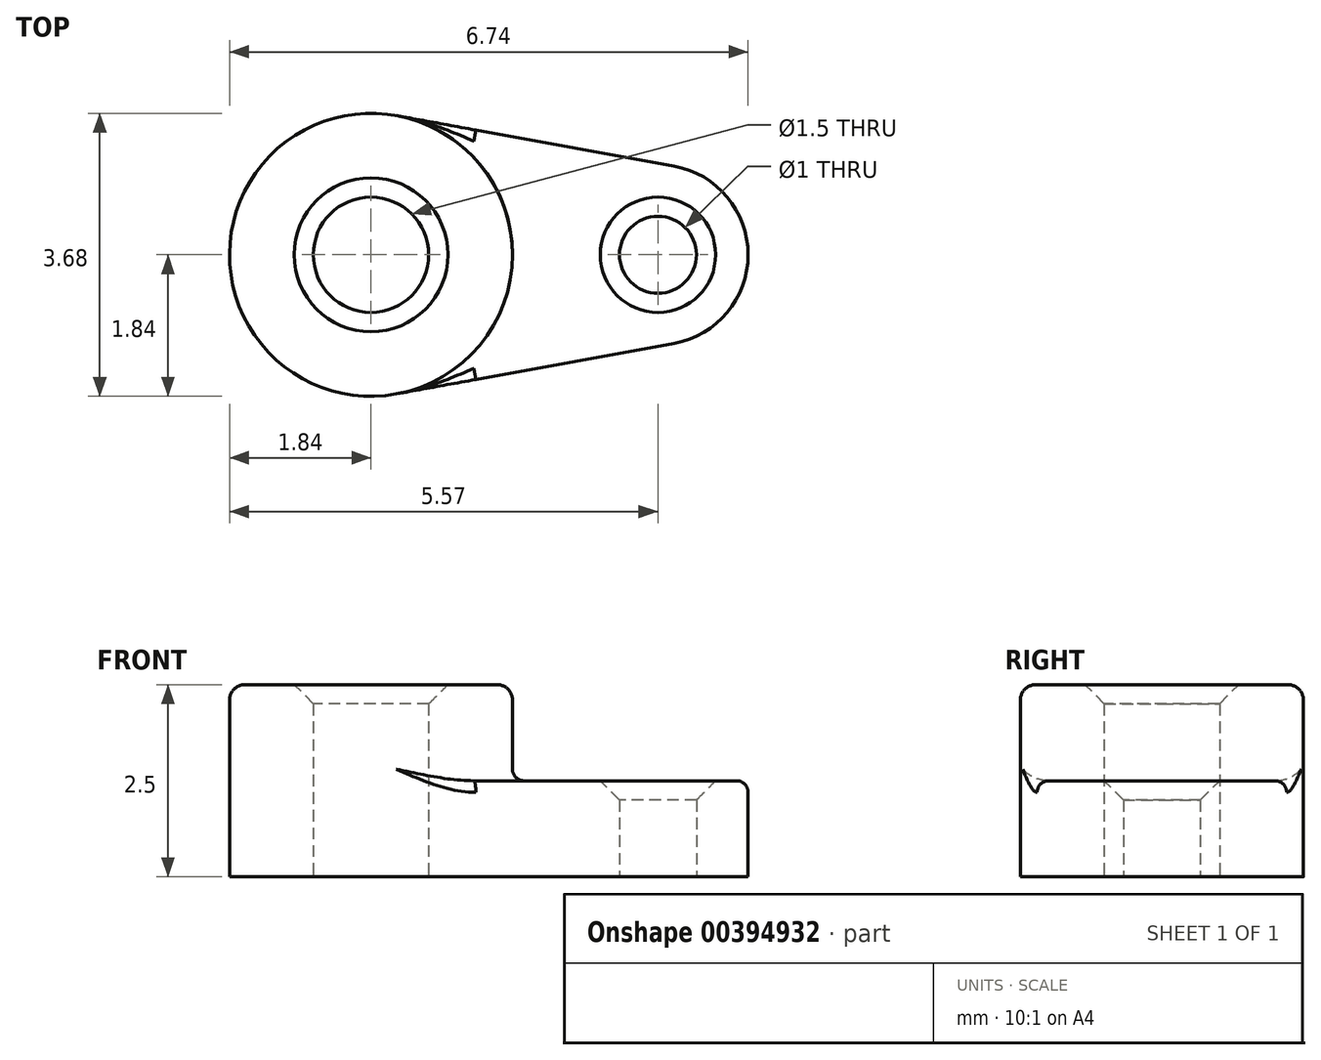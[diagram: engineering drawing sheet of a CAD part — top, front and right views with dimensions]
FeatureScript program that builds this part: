
annotation { "Feature Type Name" : "Feature", "Feature Type Description" : "" }
export const myFeature = defineFeature(function(context is Context, id is Id, definition is map)
    precondition{}
    {
        {
            var Q0;
            Q0=qCreatedBy(makeId("Top.planeOp"),FACE);
            var sketch = newSketch(context, id + "F0", { "sketchPlane" : qUnion([Q0])});
            skCircle(sketch, "E0", {"center": v(0, 0) * mm, "radius": 36.8 * mm});
            skCircle(sketch, "E1", {"center": v(74.6, 0) * mm, "radius": 23.43 * mm});
            skLineSegment(sketch, "E2", {"start": v(6.6, 36.2) * mm, "end": v(78.8, 23.05) * mm});
            skLineSegment(sketch, "E3", {"start": v(6.6, -36.2) * mm, "end": v(78.8, -23.05) * mm});
            skCircle(sketch, "E4", {"center": v(0, 0) * mm, "radius": 15 * mm});
            skCircle(sketch, "E5", {"center": v(74.6, 0) * mm, "radius": 10 * mm});
            skSolve(sketch);
        }
        {
            var Q0;
            Q0 = qSketchRegion(id + "F0", true);
            extrude(context, id + "F1", {"entities" : qUnion([Q0]), "depth" : 25 * mm});
        }
        {
            var Q0;
            Q0=makeQuery(id+"F0.imprint","IMPRINT",FACE,{"disambiguationData":[TD([[makeQuery(id+"F0.imprint","IMPRINT",EDGE,{"derivedFrom":sQuery(id+"F0.wireOp",EDGE,"E4")}),-1.0]])]});
            extrude(context, id + "F2", {"entities" : qUnion([Q0]), "operationType" : NewBodyOperationType.ADD, "depth" : 50 * mm});
        }
        {
            var Q0;
            Q0=makeQuery(id+"F2.opExtrude","CAP_EDGE",EDGE,{"disambiguationData":[OSD([sQuery(id+"F0.wireOp",EDGE,"E0")])],"isStart":false});
            fillet(context, id + "F3", {"entities" : qUnion([Q0]), "radius" : 4 * mm, "tangentPropagation" : true, "allowEdgeOverflow" : false});
        }
        {
            var Q0;
            Q0=makeQuery(id+"F2.opExtrude","CAP_EDGE",EDGE,{"disambiguationData":[OSD([sQuery(id+"F0.wireOp",EDGE,"E4")])],"isStart":false});
            var Q1;
            Q1=makeQuery(id+"F1.opExtrude","CAP_EDGE",EDGE,{"disambiguationData":[OSD([sQuery(id+"F0.wireOp",EDGE,"E5")])],"isStart":false});
            chamfer(context, id + "F4", {"entities" : qUnion([Q0, Q1]), "width" : 5 * mm, "tangentPropagation" : true});
        }
        {
            var Q0;
            {var subQ0=sQuery(id+"F0.wireOp",EDGE,"E0");Q0=makeQuery(id+"F2.boolean.opBoolean","INTERSECT",EDGE,{"derivedFrom":[makeQuery(id+"F1.opExtrude","CAP_FACE",FACE,{"disambiguationData":[OSD([subQ0,sQuery(id+"F0.wireOp",EDGE,"E1"),sQuery(id+"F0.wireOp",EDGE,"E2"),sQuery(id+"F0.wireOp",EDGE,"E3"),sQuery(id+"F0.wireOp",EDGE,"E4"),sQuery(id+"F0.wireOp",EDGE,"E5")])],"isStart":false}),makeQuery(id+"F2.opExtrude","SWEPT_FACE",FACE,{"disambiguationData":[OSD([subQ0])]})]});}
            fillet(context, id + "F5", {"entities" : qUnion([Q0]), "radius" : 3 * mm, "tangentPropagation" : true, "allowEdgeOverflow" : false});
        }
        {
            var Q0;
            Q0=makeQuery(id+"F1.opExtrude","CAP_EDGE",EDGE,{"disambiguationData":[OSD([sQuery(id+"F0.wireOp",EDGE,"E3")])],"isStart":false});
            fillet(context, id + "F6", {"entities" : qUnion([Q0]), "radius" : 3 * mm, "tangentPropagation" : true, "allowEdgeOverflow" : false});
        }
        {
            var Q0;
            Q0=makeQuery(id+"F1.opExtrude","SWEPT_BODY",BODY,{"disambiguationData":[OSD([sQuery(id+"F0.wireOp",EDGE,"E0"),sQuery(id+"F0.wireOp",EDGE,"E1"),sQuery(id+"F0.wireOp",EDGE,"E2"),sQuery(id+"F0.wireOp",EDGE,"E3"),sQuery(id+"F0.wireOp",EDGE,"E4"),sQuery(id+"F0.wireOp",EDGE,"E5")])]});
            var Q1;
            Q1=qCreatedBy(makeId("Origin.pointOp"),VERTEX);
            transform(context, id + "F7", {"entities" : qUnion([Q0]), "transformType" : TransformType.SCALE_UNIFORMLY, "scale" : .1, "scalePoint" : qUnion([Q1]), "makeCopy" : false});
        }
        {
            var Q0;
            Q0=makeQuery(id+"F1.opExtrude","SWEPT_BODY",BODY,{"disambiguationData":[OSD([sQuery(id+"F0.wireOp",EDGE,"E0"),sQuery(id+"F0.wireOp",EDGE,"E1"),sQuery(id+"F0.wireOp",EDGE,"E2"),sQuery(id+"F0.wireOp",EDGE,"E3"),sQuery(id+"F0.wireOp",EDGE,"E4"),sQuery(id+"F0.wireOp",EDGE,"E5")])]});
            var Q1;
            Q1=qCreatedBy(makeId("Origin.pointOp"),VERTEX);
            transform(context, id + "F8", {"entities" : qUnion([Q0]), "transformType" : TransformType.SCALE_UNIFORMLY, "scale" : .5, "scalePoint" : qUnion([Q1]), "makeCopy" : false});
        }
    });
